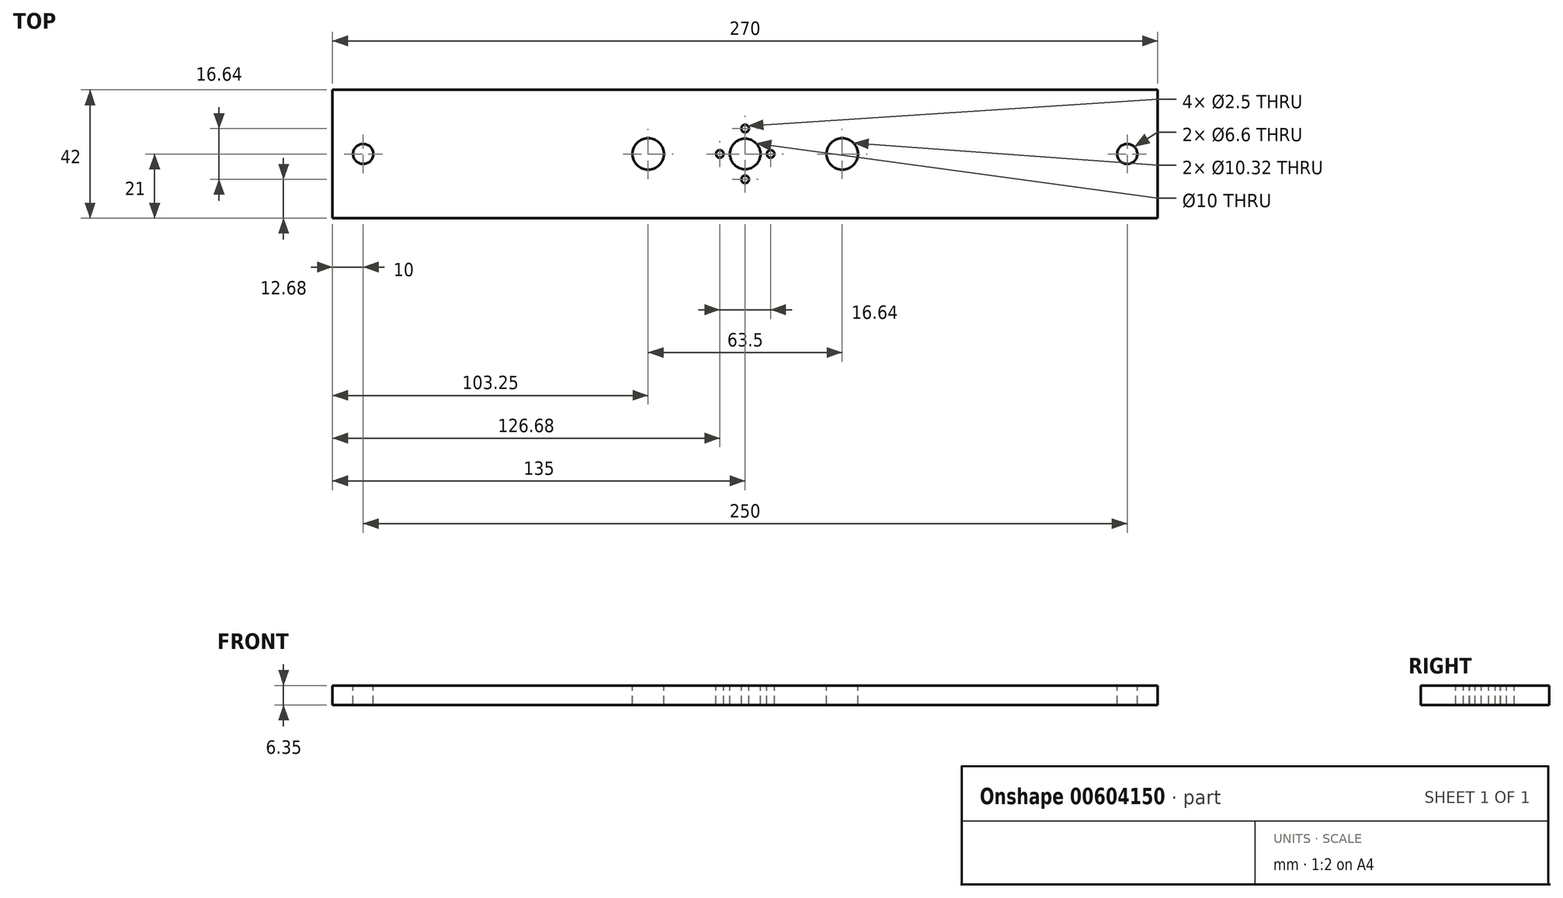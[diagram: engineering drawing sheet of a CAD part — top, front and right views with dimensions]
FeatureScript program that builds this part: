
annotation { "Feature Type Name" : "Feature", "Feature Type Description" : "" }
export const myFeature = defineFeature(function(context is Context, id is Id, definition is map)
    precondition{}
    {
        {
            var Q0;
            Q0=qCreatedBy(makeId("Top.planeOp"),FACE);
            var sketch = newSketch(context, id + "F0", { "sketchPlane" : qUnion([Q0])});
            skLineSegment(sketch, "E0.bottom", {"start": v(0, 0) * mm, "end": v(270, 0) * mm});
            skLineSegment(sketch, "E0.top", {"start": v(0, 42) * mm, "end": v(270, 42) * mm});
            skLineSegment(sketch, "E0.left", {"start": v(0, 0) * mm, "end": v(0, 42) * mm});
            skLineSegment(sketch, "E0.right", {"start": v(270, 0) * mm, "end": v(270, 42) * mm});
            skSolve(sketch);
        }
        {
            var Q0;
            Q0=makeQuery(id+"F0.imprint","IMPRINT",FACE,{"disambiguationData":[TD([[makeQuery(id+"F0.imprint","IMPRINT",EDGE,{"derivedFrom":sQuery(id+"F0.wireOp",EDGE,"E0.bottom")}),1.0]])]});
            extrude(context, id + "F1", {"entities" : qUnion([Q0]), "depth" : 6.35 * mm, "offsetDistance" : 25 * mm});
        }
        {
            var Q0;
            Q0=makeQuery(id+"F1.opExtrude","CAP_FACE",FACE,{"disambiguationData":[OSD([sQuery(id+"F0.wireOp",EDGE,"E0.bottom"),sQuery(id+"F0.wireOp",EDGE,"E0.top"),sQuery(id+"F0.wireOp",EDGE,"E0.left"),sQuery(id+"F0.wireOp",EDGE,"E0.right")])],"isStart":false});
            var sketch = newSketch(context, id + "F2", { "sketchPlane" : qUnion([Q0])});
            skCircle(sketch, "E1", {"center": v(135, 21) * mm, "radius": 5 * mm});
            skSolve(sketch);
        }
        {
            var Q0;
            Q0 = qSketchRegion(id + "F2", true);
            extrude(context, id + "F3", {"entities" : qUnion([Q0]), "operationType" : NewBodyOperationType.REMOVE, "endBound" : BoundingType.THROUGH_ALL, "oppositeDirection" : true, "depth" : 25 * mm, "offsetDistance" : 25 * mm});
        }
        {
            var Q0;
            Q0=makeQuery(id+"F1.opExtrude","CAP_FACE",FACE,{"disambiguationData":[OSD([sQuery(id+"F0.wireOp",EDGE,"E0.bottom"),sQuery(id+"F0.wireOp",EDGE,"E0.top"),sQuery(id+"F0.wireOp",EDGE,"E0.left"),sQuery(id+"F0.wireOp",EDGE,"E0.right")])],"isStart":false});
            var sketch = newSketch(context, id + "F4", { "sketchPlane" : qUnion([Q0])});
            skCircle(sketch, "E2", {"center": v(10, 21) * mm, "radius": 3.3 * mm});
            skCircle(sketch, "E3", {"center": v(260, 21) * mm, "radius": 3.3 * mm});
            skSolve(sketch);
        }
        {
            var Q0;
            Q0 = qSketchRegion(id + "F4", true);
            extrude(context, id + "F5", {"entities" : qUnion([Q0]), "operationType" : NewBodyOperationType.REMOVE, "endBound" : BoundingType.THROUGH_ALL, "oppositeDirection" : true, "depth" : 25 * mm, "offsetDistance" : 25 * mm});
        }
        {
            var Q0;
            Q0=makeQuery(id+"F1.opExtrude","CAP_FACE",FACE,{"disambiguationData":[OSD([sQuery(id+"F0.wireOp",EDGE,"E0.bottom"),sQuery(id+"F0.wireOp",EDGE,"E0.top"),sQuery(id+"F0.wireOp",EDGE,"E0.left"),sQuery(id+"F0.wireOp",EDGE,"E0.right")])],"isStart":false});
            var sketch = newSketch(context, id + "F6", { "sketchPlane" : qUnion([Q0])});
            skCircle(sketch, "E4", {"center": v(103.25, 21) * mm, "radius": 5.16 * mm});
            skCircle(sketch, "E5", {"center": v(166.75, 21) * mm, "radius": 5.16 * mm});
            skSolve(sketch);
        }
        {
            var Q0;
            Q0 = qSketchRegion(id + "F6", true);
            extrude(context, id + "F7", {"entities" : qUnion([Q0]), "operationType" : NewBodyOperationType.REMOVE, "endBound" : BoundingType.THROUGH_ALL, "oppositeDirection" : true, "depth" : 25 * mm, "offsetDistance" : 25 * mm});
        }
        {
            var Q0;
            Q0=makeQuery(id+"F1.opExtrude","CAP_FACE",FACE,{"disambiguationData":[OSD([sQuery(id+"F0.wireOp",EDGE,"E0.bottom"),sQuery(id+"F0.wireOp",EDGE,"E0.top"),sQuery(id+"F0.wireOp",EDGE,"E0.left"),sQuery(id+"F0.wireOp",EDGE,"E0.right")])],"isStart":false});
            var sketch = newSketch(context, id + "F8", { "sketchPlane" : qUnion([Q0])});
            skCircle(sketch, "E6", {"center": v(135, 29.32) * mm, "radius": 1.25 * mm});
            skCircle(sketch, "E7.1.0", {"center": v(126.68, 21) * mm, "radius": 1.25 * mm});
            skCircle(sketch, "E7.2.0", {"center": v(135, 12.68) * mm, "radius": 1.25 * mm});
            skCircle(sketch, "E7.3.0", {"center": v(143.32, 21) * mm, "radius": 1.25 * mm});
            skPoint(sketch, "E7.center", {"position": v(135, 21) * mm});
            skSolve(sketch);
        }
        {
            var Q0;
            Q0 = qSketchRegion(id + "F8", true);
            extrude(context, id + "F9", {"entities" : qUnion([Q0]), "operationType" : NewBodyOperationType.REMOVE, "endBound" : BoundingType.THROUGH_ALL, "oppositeDirection" : true, "depth" : 25 * mm, "offsetDistance" : 25 * mm});
        }
    });
